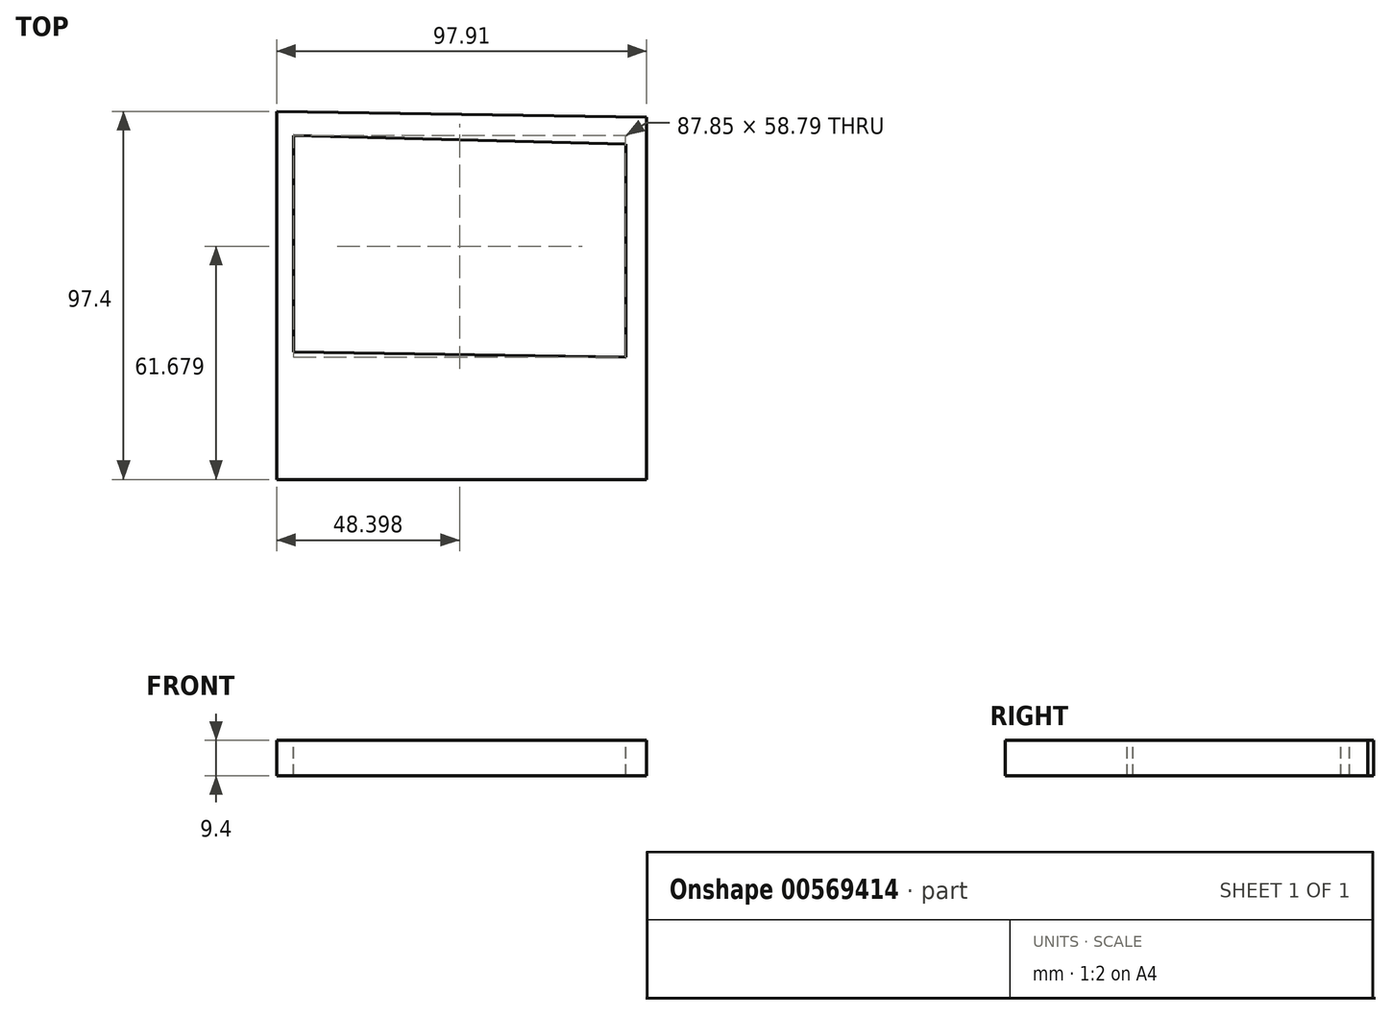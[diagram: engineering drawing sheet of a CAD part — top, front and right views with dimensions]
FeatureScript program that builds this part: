
annotation { "Feature Type Name" : "Feature", "Feature Type Description" : "" }
export const myFeature = defineFeature(function(context is Context, id is Id, definition is map)
    precondition{}
    {
        {
            var Q0;
            Q0=qCreatedBy(makeId("Top.planeOp"),FACE);
            var sketch = newSketch(context, id + "F0", { "sketchPlane" : qUnion([Q0])});
            skLineSegment(sketch, "E0", {"start": v(-57.5, 42.87) * mm, "end": v(-57.5, -29.13) * mm});
            skLineSegment(sketch, "E1", {"start": v(-57.5, -29.13) * mm, "end": v(40.42, -29.13) * mm});
            skLineSegment(sketch, "E2", {"start": v(40.42, -29.13) * mm, "end": v(40.42, 41.3) * mm});
            skLineSegment(sketch, "E3", {"start": v(40.42, 41.3) * mm, "end": v(-57.5, 42.87) * mm});
            skLineSegment(sketch, "E4", {"start": v(40.42, 41.3) * mm, "end": v(40.42, 42.87) * mm});
            skLineSegment(sketch, "E5", {"start": v(40.42, 42.87) * mm, "end": v(40.42, 27.84) * mm});
            skLineSegment(sketch, "E6", {"start": v(-53.02, 36.54) * mm, "end": v(-53.02, -20.82) * mm});
            skLineSegment(sketch, "E7", {"start": v(-53.02, -20.82) * mm, "end": v(34.83, -22.24) * mm});
            skLineSegment(sketch, "E8", {"start": v(34.83, -22.24) * mm, "end": v(34.83, 34.17) * mm});
            skLineSegment(sketch, "E9", {"start": v(34.83, 34.17) * mm, "end": v(-53.02, 36.54) * mm});
            skLineSegment(sketch, "E10", {"start": v(-47.42, 31.4) * mm, "end": v(-47.42, -11.33) * mm});
            skLineSegment(sketch, "E11", {"start": v(-47.42, -11.33) * mm, "end": v(29.8, -12.58) * mm});
            skLineSegment(sketch, "E12", {"start": v(29.8, -12.58) * mm, "end": v(29.8, 27.84) * mm});
            skLineSegment(sketch, "E13", {"start": v(29.8, 27.84) * mm, "end": v(-47.42, 31.4) * mm});
            skLineSegment(sketch, "E14", {"start": v(-41.55, 27.84) * mm, "end": v(-41.55, -6.58) * mm});
            skLineSegment(sketch, "E15", {"start": v(-41.55, -6.58) * mm, "end": v(25.29, -7.66) * mm});
            skLineSegment(sketch, "E16", {"start": v(25.29, -7.66) * mm, "end": v(25.29, 23.1) * mm});
            skLineSegment(sketch, "E17", {"start": v(25.29, 23.1) * mm, "end": v(-41.55, 27.84) * mm});
            skLineSegment(sketch, "E18", {"start": v(-41.55, 27.84) * mm, "end": v(-41.55, 20.32) * mm});
            skLineSegment(sketch, "E19", {"start": v(-41.55, 27.84) * mm, "end": v(-41.55, 23.1) * mm});
            skLineSegment(sketch, "E20", {"start": v(-34, 20.32) * mm, "end": v(-34, 0) * mm});
            skLineSegment(sketch, "E21", {"start": v(-34, 0) * mm, "end": v(19.42, -0.86) * mm});
            skLineSegment(sketch, "E22", {"start": v(19.42, -0.86) * mm, "end": v(19.42, 16.76) * mm});
            skLineSegment(sketch, "E23", {"start": v(19.42, 16.76) * mm, "end": v(-34, 20.32) * mm});
            skLineSegment(sketch, "E24", {"start": v(-26.16, 15.97) * mm, "end": v(-26.16, 6.87) * mm});
            skLineSegment(sketch, "E25", {"start": v(-26.16, 6.87) * mm, "end": v(15.42, 4.95) * mm});
            skLineSegment(sketch, "E26", {"start": v(15.42, 4.95) * mm, "end": v(15.42, 12.01) * mm});
            skLineSegment(sketch, "E27", {"start": v(15.42, 12.01) * mm, "end": v(-26.16, 15.97) * mm});
            skSolve(sketch);
        }
        {
            var Q0;
            Q0 = qSketchRegion(id + "F0", true);
            extrude(context, id + "F1", {"entities" : qUnion([Q0]), "oppositeDirection" : true, "depth" : 9.4 * mm, "offsetDistance" : 25.4 * mm});
        }
        {
            var Q0;
            Q0=makeQuery(id+"F1.opExtrude","SWEPT_FACE",FACE,{"disambiguationData":[OSD([sQuery(id+"F0.wireOp",EDGE,"E1")])]});
            extrude(context, id + "F2", {"entities" : qUnion([Q0]), "operationType" : NewBodyOperationType.ADD, "depth" : 25.4 * mm, "offsetDistance" : 25.4 * mm});
        }
    });
